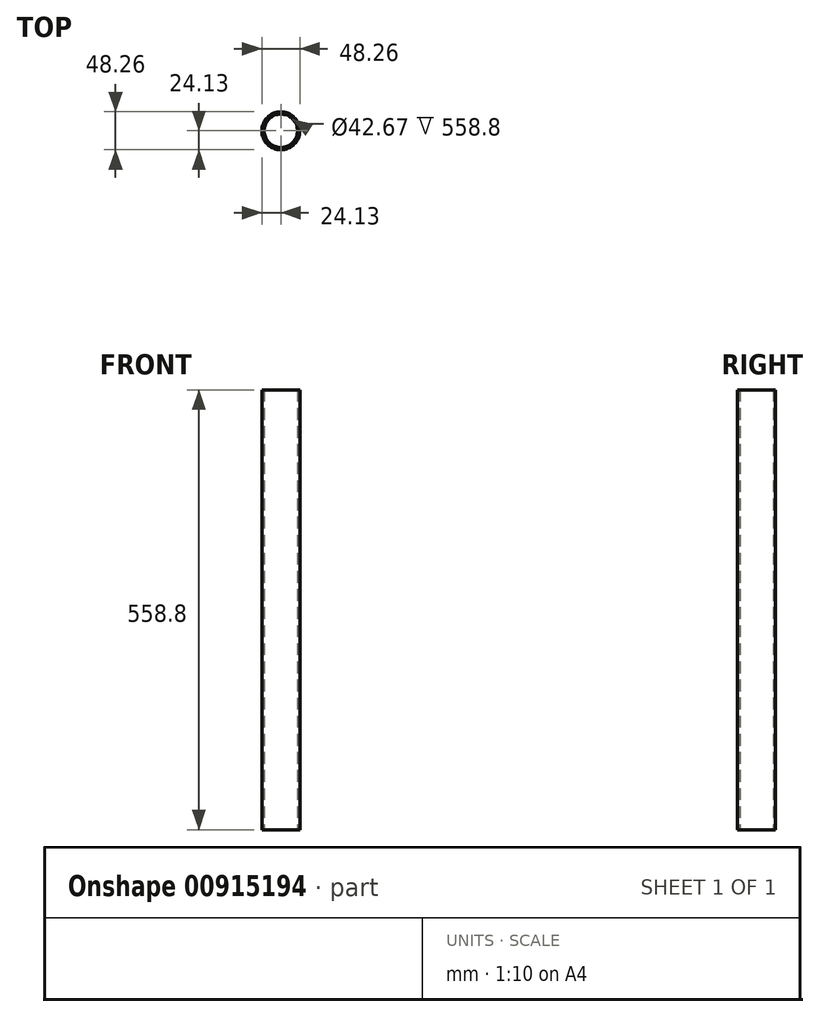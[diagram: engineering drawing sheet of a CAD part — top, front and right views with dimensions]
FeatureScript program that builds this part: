
annotation { "Feature Type Name" : "Feature", "Feature Type Description" : "" }
export const myFeature = defineFeature(function(context is Context, id is Id, definition is map)
    precondition{}
    {
        {
            var Q0;
            Q0=qCreatedBy(makeId("Top.planeOp"),FACE);
            var sketch = newSketch(context, id + "F0", { "sketchPlane" : qUnion([Q0])});
            skCircle(sketch, "E0", {"center": v(0, 0) * mm, "radius": 24.13 * mm});
            skCircle(sketch, "E1", {"center": v(0, 0) * mm, "radius": 21.34 * mm});
            skSolve(sketch);
        }
        {
            var Q0;
            Q0=makeQuery(id+"F0.imprint","IMPRINT",FACE,{"disambiguationData":[TD([[makeQuery(id+"F0.imprint","IMPRINT",EDGE,{"derivedFrom":sQuery(id+"F0.wireOp",EDGE,"E0")}),1.0]])]});
            extrude(context, id + "F1", {"entities" : qUnion([Q0]), "depth" : 558.8 * mm, "offsetDistance" : 25.4 * mm});
        }
    });
